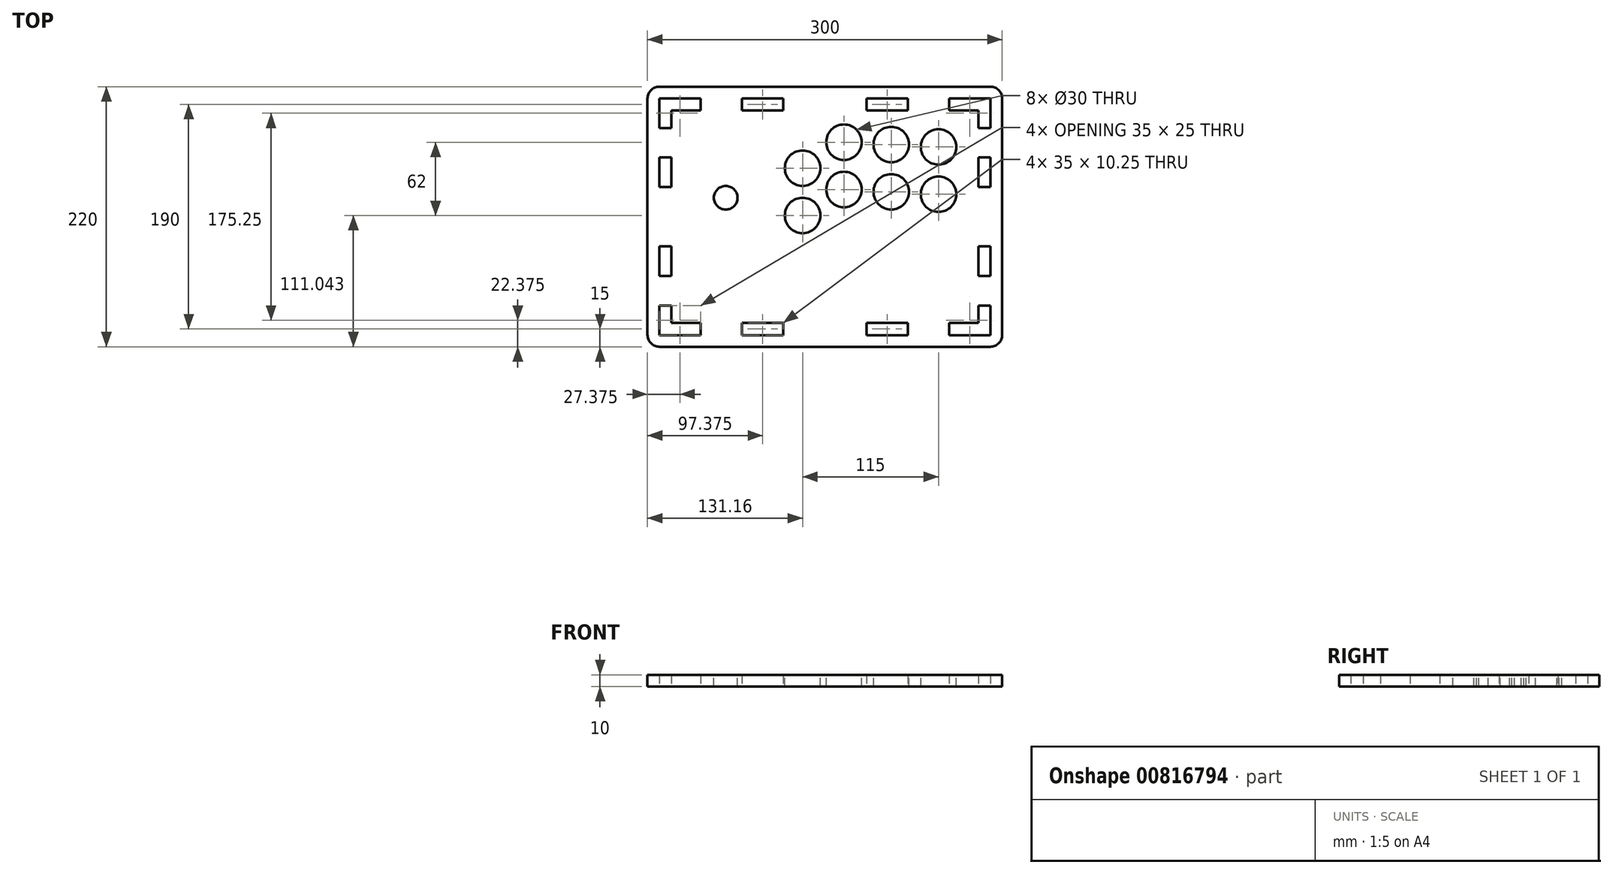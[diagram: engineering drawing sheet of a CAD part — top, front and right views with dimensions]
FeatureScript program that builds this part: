
annotation { "Feature Type Name" : "Feature", "Feature Type Description" : "" }
export const myFeature = defineFeature(function(context is Context, id is Id, definition is map)
    precondition{}
    {
        {
            var Q0;
            Q0=qCreatedBy(makeId("Top.planeOp"),FACE);
            var sketch = newSketch(context, id + "F0", { "sketchPlane" : qUnion([Q0])});
            skLineSegment(sketch, "E0.bottom", {"start": v(-140, 110) * mm, "end": v(140, 110) * mm});
            skLineSegment(sketch, "E0.top", {"start": v(-140, -110) * mm, "end": v(140, -110) * mm});
            skLineSegment(sketch, "E0.left", {"start": v(-150, 100) * mm, "end": v(-150, -100) * mm});
            skLineSegment(sketch, "E0.right", {"start": v(150, 100) * mm, "end": v(150, -100) * mm});
            skPoint(sketch, "E1.middle", {"position": v(0, 0) * mm});
            skLineSegment(sketch, "E2", {"start": v(-140.12, -100.12) * mm, "end": v(-105.13, -100.12) * mm});
            skLineSegment(sketch, "E3", {"start": v(-140.12, -100.12) * mm, "end": v(-140.13, -75.12) * mm});
            skLineSegment(sketch, "E4", {"start": v(-140.12, -75.12) * mm, "end": v(-129.88, -75.12) * mm});
            skLineSegment(sketch, "E5", {"start": v(-129.88, -75.12) * mm, "end": v(-129.88, -89.88) * mm});
            skLineSegment(sketch, "E6", {"start": v(-140.12, -50.12) * mm, "end": v(-129.88, -50.12) * mm});
            skLineSegment(sketch, "E7", {"start": v(-129.88, -50.12) * mm, "end": v(-129.88, -25.12) * mm});
            skLineSegment(sketch, "E8", {"start": v(-129.88, -25.12) * mm, "end": v(-140.12, -25.12) * mm});
            skLineSegment(sketch, "E9", {"start": v(-140.12, -25.12) * mm, "end": v(-140.12, -50.12) * mm});
            skLineSegment(sketch, "E10", {"start": v(-105.13, -100.12) * mm, "end": v(-105.13, -89.87) * mm});
            skLineSegment(sketch, "E11", {"start": v(-105.13, -89.87) * mm, "end": v(-129.88, -89.88) * mm});
            skLineSegment(sketch, "E12.MirrorCS", {"start": v(140.12, -75.12) * mm, "end": v(129.88, -75.12) * mm});
            skLineSegment(sketch, "E13.MirrorCS", {"start": v(129.88, -75.12) * mm, "end": v(129.88, -89.88) * mm});
            skLineSegment(sketch, "E14.MirrorCS", {"start": v(105.13, -89.87) * mm, "end": v(129.88, -89.88) * mm});
            skLineSegment(sketch, "E15.MirrorCS", {"start": v(105.13, -100.12) * mm, "end": v(105.13, -89.87) * mm});
            skLineSegment(sketch, "E16.MirrorCS", {"start": v(140.12, -100.12) * mm, "end": v(105.13, -100.12) * mm});
            skLineSegment(sketch, "E17.MirrorCS", {"start": v(140.12, -100.12) * mm, "end": v(140.13, -75.12) * mm});
            skLineSegment(sketch, "E18", {"start": v(-70.13, -100.12) * mm, "end": v(-70.13, -89.87) * mm});
            skLineSegment(sketch, "E19", {"start": v(-70.13, -89.87) * mm, "end": v(-35.13, -89.87) * mm});
            skLineSegment(sketch, "E20", {"start": v(-35.13, -89.87) * mm, "end": v(-35.13, -100.12) * mm});
            skLineSegment(sketch, "E21", {"start": v(-70.13, -100.12) * mm, "end": v(-35.13, -100.12) * mm});
            skLineSegment(sketch, "E22.MirrorCS", {"start": v(70.13, -89.87) * mm, "end": v(35.13, -89.87) * mm});
            skLineSegment(sketch, "E23.MirrorCS", {"start": v(70.13, -100.12) * mm, "end": v(70.13, -89.87) * mm});
            skLineSegment(sketch, "E24.MirrorCS", {"start": v(70.13, -100.12) * mm, "end": v(35.13, -100.12) * mm});
            skLineSegment(sketch, "E25.MirrorCS", {"start": v(35.13, -89.87) * mm, "end": v(35.13, -100.12) * mm});
            skLineSegment(sketch, "E26.MirrorCS", {"start": v(105.13, 100.12) * mm, "end": v(105.13, 89.87) * mm});
            skLineSegment(sketch, "E27.MirrorCS", {"start": v(-70.13, 100.12) * mm, "end": v(-70.13, 89.87) * mm});
            skLineSegment(sketch, "E28.MirrorCS", {"start": v(140.12, 75.12) * mm, "end": v(129.88, 75.12) * mm});
            skLineSegment(sketch, "E29.MirrorCS", {"start": v(70.13, 100.12) * mm, "end": v(70.13, 89.87) * mm});
            skLineSegment(sketch, "E30.MirrorCS", {"start": v(-35.13, 89.87) * mm, "end": v(-35.13, 100.12) * mm});
            skLineSegment(sketch, "E31.MirrorCS", {"start": v(-140.12, 75.12) * mm, "end": v(-129.88, 75.12) * mm});
            skLineSegment(sketch, "E32.MirrorCS", {"start": v(35.13, 89.87) * mm, "end": v(35.13, 100.12) * mm});
            skLineSegment(sketch, "E33.MirrorCS", {"start": v(-105.13, 100.12) * mm, "end": v(-105.13, 89.87) * mm});
            skLineSegment(sketch, "E34.MirrorCS", {"start": v(140.12, 100.12) * mm, "end": v(105.13, 100.12) * mm});
            skLineSegment(sketch, "E35.MirrorCS", {"start": v(-140.12, 100.12) * mm, "end": v(-140.13, 75.12) * mm});
            skLineSegment(sketch, "E36.MirrorCS", {"start": v(-70.13, 100.12) * mm, "end": v(-35.13, 100.12) * mm});
            skLineSegment(sketch, "E37.MirrorCS", {"start": v(-105.13, 89.87) * mm, "end": v(-129.88, 89.88) * mm});
            skLineSegment(sketch, "E38.MirrorCS", {"start": v(-140.12, 100.12) * mm, "end": v(-105.13, 100.12) * mm});
            skLineSegment(sketch, "E39.MirrorCS", {"start": v(-70.13, 89.87) * mm, "end": v(-35.13, 89.87) * mm});
            skLineSegment(sketch, "E40.MirrorCS", {"start": v(129.88, 75.12) * mm, "end": v(129.88, 89.88) * mm});
            skLineSegment(sketch, "E41.MirrorCS", {"start": v(70.13, 100.12) * mm, "end": v(35.13, 100.12) * mm});
            skLineSegment(sketch, "E42.MirrorCS", {"start": v(70.13, 89.87) * mm, "end": v(35.13, 89.87) * mm});
            skLineSegment(sketch, "E43.MirrorCS", {"start": v(105.13, 89.87) * mm, "end": v(129.88, 89.88) * mm});
            skLineSegment(sketch, "E44.MirrorCS", {"start": v(-129.88, 75.12) * mm, "end": v(-129.88, 89.88) * mm});
            skLineSegment(sketch, "E45.MirrorCS", {"start": v(140.12, 100.12) * mm, "end": v(140.13, 75.12) * mm});
            skLineSegment(sketch, "E46.MirrorCS", {"start": v(-129.88, 25.12) * mm, "end": v(-140.12, 25.12) * mm});
            skLineSegment(sketch, "E47.MirrorCS", {"start": v(-140.12, 25.12) * mm, "end": v(-140.12, 50.12) * mm});
            skLineSegment(sketch, "E48.MirrorCS", {"start": v(-140.12, 50.12) * mm, "end": v(-129.88, 50.12) * mm});
            skLineSegment(sketch, "E49.MirrorCS", {"start": v(-129.88, 50.12) * mm, "end": v(-129.88, 25.12) * mm});
            skLineSegment(sketch, "E50.MirrorCS", {"start": v(140.12, 50.12) * mm, "end": v(129.88, 50.12) * mm});
            skLineSegment(sketch, "E51.MirrorCS", {"start": v(140.12, 25.12) * mm, "end": v(140.12, 50.12) * mm});
            skLineSegment(sketch, "E52.MirrorCS", {"start": v(129.88, 50.12) * mm, "end": v(129.88, 25.12) * mm});
            skLineSegment(sketch, "E53.MirrorCS", {"start": v(129.88, 25.12) * mm, "end": v(140.12, 25.12) * mm});
            skLineSegment(sketch, "E54.MirrorCS", {"start": v(129.88, -25.12) * mm, "end": v(140.12, -25.12) * mm});
            skLineSegment(sketch, "E55.MirrorCS", {"start": v(140.12, -25.12) * mm, "end": v(140.12, -50.12) * mm});
            skLineSegment(sketch, "E56.MirrorCS", {"start": v(140.12, -50.12) * mm, "end": v(129.88, -50.12) * mm});
            skLineSegment(sketch, "E57.MirrorCS", {"start": v(129.88, -50.12) * mm, "end": v(129.88, -25.12) * mm});
            skPoint(sketch, "E58.visualSharp", {"position": v(-150, 110) * mm});
            skArc(sketch, "E58.filletArc", {"start": v(-140, 110) * mm, "mid": v(-147.07, 107.07) * mm, "end": v(-150, 100) * mm});
            skPoint(sketch, "E59.visualSharp", {"position": v(-150, -110) * mm});
            skArc(sketch, "E59.filletArc", {"start": v(-150, -100) * mm, "mid": v(-147.07, -107.07) * mm, "end": v(-140, -110) * mm});
            skPoint(sketch, "E60.visualSharp", {"position": v(150, -110) * mm});
            skArc(sketch, "E60.filletArc", {"start": v(140, -110) * mm, "mid": v(147.07, -107.07) * mm, "end": v(150, -100) * mm});
            skPoint(sketch, "E61.visualSharp", {"position": v(150, 110) * mm});
            skArc(sketch, "E61.filletArc", {"start": v(150, 100) * mm, "mid": v(147.07, 107.07) * mm, "end": v(140, 110) * mm});
            skSolve(sketch);
        }
        {
            var Q0;
            Q0=makeQuery(id+"F0.imprint","IMPRINT",FACE,{"disambiguationData":[TD([[makeQuery(id+"F0.imprint","IMPRINT",EDGE,{"derivedFrom":sQuery(id+"F0.wireOp",EDGE,"E0.bottom")}),-1.0]])]});
            extrude(context, id + "F1", {"entities" : qUnion([Q0]), "depth" : 10 * mm, "offsetDistance" : 25 * mm});
        }
        {
            var Q0;
            Q0=makeQuery(id+"F1.opExtrude","CAP_FACE",FACE,{"disambiguationData":[OSD([sQuery(id+"F0.wireOp",EDGE,"E0.bottom"),sQuery(id+"F0.wireOp",EDGE,"E0.top"),sQuery(id+"F0.wireOp",EDGE,"E0.left"),sQuery(id+"F0.wireOp",EDGE,"E0.right"),sQuery(id+"F0.wireOp",EDGE,"E2"),sQuery(id+"F0.wireOp",EDGE,"E3"),sQuery(id+"F0.wireOp",EDGE,"E4"),sQuery(id+"F0.wireOp",EDGE,"E5"),sQuery(id+"F0.wireOp",EDGE,"E6"),sQuery(id+"F0.wireOp",EDGE,"E7"),sQuery(id+"F0.wireOp",EDGE,"E8"),sQuery(id+"F0.wireOp",EDGE,"E9"),sQuery(id+"F0.wireOp",EDGE,"E10"),sQuery(id+"F0.wireOp",EDGE,"E11"),sQuery(id+"F0.wireOp",EDGE,"E12.MirrorCS"),sQuery(id+"F0.wireOp",EDGE,"E13.MirrorCS"),sQuery(id+"F0.wireOp",EDGE,"E14.MirrorCS"),sQuery(id+"F0.wireOp",EDGE,"E15.MirrorCS"),sQuery(id+"F0.wireOp",EDGE,"E16.MirrorCS"),sQuery(id+"F0.wireOp",EDGE,"E17.MirrorCS"),sQuery(id+"F0.wireOp",EDGE,"E18"),sQuery(id+"F0.wireOp",EDGE,"E19"),sQuery(id+"F0.wireOp",EDGE,"E20"),sQuery(id+"F0.wireOp",EDGE,"E21"),sQuery(id+"F0.wireOp",EDGE,"E22.MirrorCS"),sQuery(id+"F0.wireOp",EDGE,"E23.MirrorCS"),sQuery(id+"F0.wireOp",EDGE,"E24.MirrorCS"),sQuery(id+"F0.wireOp",EDGE,"E25.MirrorCS"),sQuery(id+"F0.wireOp",EDGE,"E26.MirrorCS"),sQuery(id+"F0.wireOp",EDGE,"E27.MirrorCS"),sQuery(id+"F0.wireOp",EDGE,"E28.MirrorCS"),sQuery(id+"F0.wireOp",EDGE,"E29.MirrorCS"),sQuery(id+"F0.wireOp",EDGE,"E30.MirrorCS"),sQuery(id+"F0.wireOp",EDGE,"E31.MirrorCS"),sQuery(id+"F0.wireOp",EDGE,"E32.MirrorCS"),sQuery(id+"F0.wireOp",EDGE,"E33.MirrorCS"),sQuery(id+"F0.wireOp",EDGE,"E34.MirrorCS"),sQuery(id+"F0.wireOp",EDGE,"E35.MirrorCS"),sQuery(id+"F0.wireOp",EDGE,"E36.MirrorCS"),sQuery(id+"F0.wireOp",EDGE,"E37.MirrorCS"),sQuery(id+"F0.wireOp",EDGE,"E38.MirrorCS"),sQuery(id+"F0.wireOp",EDGE,"E39.MirrorCS"),sQuery(id+"F0.wireOp",EDGE,"E40.MirrorCS"),sQuery(id+"F0.wireOp",EDGE,"E41.MirrorCS"),sQuery(id+"F0.wireOp",EDGE,"E42.MirrorCS"),sQuery(id+"F0.wireOp",EDGE,"E43.MirrorCS"),sQuery(id+"F0.wireOp",EDGE,"E44.MirrorCS"),sQuery(id+"F0.wireOp",EDGE,"E45.MirrorCS"),sQuery(id+"F0.wireOp",EDGE,"E46.MirrorCS"),sQuery(id+"F0.wireOp",EDGE,"E47.MirrorCS"),sQuery(id+"F0.wireOp",EDGE,"E48.MirrorCS"),sQuery(id+"F0.wireOp",EDGE,"E49.MirrorCS"),sQuery(id+"F0.wireOp",EDGE,"E50.MirrorCS"),sQuery(id+"F0.wireOp",EDGE,"E51.MirrorCS"),sQuery(id+"F0.wireOp",EDGE,"E52.MirrorCS"),sQuery(id+"F0.wireOp",EDGE,"E53.MirrorCS"),sQuery(id+"F0.wireOp",EDGE,"E54.MirrorCS"),sQuery(id+"F0.wireOp",EDGE,"E55.MirrorCS"),sQuery(id+"F0.wireOp",EDGE,"E56.MirrorCS"),sQuery(id+"F0.wireOp",EDGE,"E57.MirrorCS")])],"isStart":false});
            var sketch = newSketch(context, id + "F2", { "sketchPlane" : qUnion([Q0])});
            skLineSegment(sketch, "E62.bottom", {"start": v(-150, 110) * mm, "end": v(150, 110) * mm});
            skLineSegment(sketch, "E62.top", {"start": v(-150, -110) * mm, "end": v(150, -110) * mm});
            skLineSegment(sketch, "E62.left", {"start": v(-150, 110) * mm, "end": v(-150, -110) * mm});
            skLineSegment(sketch, "E62.right", {"start": v(150, 110) * mm, "end": v(150, -110) * mm});
            skPoint(sketch, "E62.middle", {"position": v(0, 0) * mm});
            skLineSegment(sketch, "E63", {"start": v(150, -110) * mm, "end": v(-69, -110) * mm});
            skCircle(sketch, "E64", {"center": v(96.16, 19.04) * mm, "radius": 15 * mm});
            skCircle(sketch, "E65", {"center": v(96.16, 59.04) * mm, "radius": 15 * mm});
            skCircle(sketch, "E66", {"center": v(56.16, 61.04) * mm, "radius": 15 * mm});
            skCircle(sketch, "E67", {"center": v(56.16, 21.04) * mm, "radius": 15 * mm});
            skCircle(sketch, "E68", {"center": v(16.16, 23.04) * mm, "radius": 15 * mm});
            skCircle(sketch, "E69", {"center": v(16.16, 63.04) * mm, "radius": 15 * mm});
            skCircle(sketch, "E70", {"center": v(-18.84, 1.04) * mm, "radius": 15 * mm});
            skCircle(sketch, "E71", {"center": v(-18.84, 41.04) * mm, "radius": 15 * mm});
            skCircle(sketch, "E72", {"center": v(-83.84, 16.04) * mm, "radius": 10 * mm});
            skSolve(sketch);
        }
        {
            var Q0;
            Q0=makeQuery(id+"F2.imprint","IMPRINT",FACE,{"disambiguationData":[TD([[makeQuery(id+"F2.imprint","IMPRINT",EDGE,{"derivedFrom":sQuery(id+"F2.wireOp",EDGE,"E72")}),1.0]])]});
            var Q1;
            Q1=makeQuery(id+"F2.imprint","IMPRINT",FACE,{"disambiguationData":[TD([[makeQuery(id+"F2.imprint","IMPRINT",EDGE,{"derivedFrom":sQuery(id+"F2.wireOp",EDGE,"E71")}),1.0]])]});
            var Q2;
            Q2=makeQuery(id+"F2.imprint","IMPRINT",FACE,{"disambiguationData":[TD([[makeQuery(id+"F2.imprint","IMPRINT",EDGE,{"derivedFrom":sQuery(id+"F2.wireOp",EDGE,"E69")}),1.0]])]});
            var Q3;
            Q3=makeQuery(id+"F2.imprint","IMPRINT",FACE,{"disambiguationData":[TD([[makeQuery(id+"F2.imprint","IMPRINT",EDGE,{"derivedFrom":sQuery(id+"F2.wireOp",EDGE,"E66")}),1.0]])]});
            var Q4;
            Q4=makeQuery(id+"F2.imprint","IMPRINT",FACE,{"disambiguationData":[TD([[makeQuery(id+"F2.imprint","IMPRINT",EDGE,{"derivedFrom":sQuery(id+"F2.wireOp",EDGE,"E65")}),1.0]])]});
            var Q5;
            Q5=makeQuery(id+"F2.imprint","IMPRINT",FACE,{"disambiguationData":[TD([[makeQuery(id+"F2.imprint","IMPRINT",EDGE,{"derivedFrom":sQuery(id+"F2.wireOp",EDGE,"E64")}),1.0]])]});
            var Q6;
            Q6=makeQuery(id+"F2.imprint","IMPRINT",FACE,{"disambiguationData":[TD([[makeQuery(id+"F2.imprint","IMPRINT",EDGE,{"derivedFrom":sQuery(id+"F2.wireOp",EDGE,"E67")}),1.0]])]});
            var Q7;
            Q7=makeQuery(id+"F2.imprint","IMPRINT",FACE,{"disambiguationData":[TD([[makeQuery(id+"F2.imprint","IMPRINT",EDGE,{"derivedFrom":sQuery(id+"F2.wireOp",EDGE,"E68")}),1.0]])]});
            var Q8;
            Q8=makeQuery(id+"F2.imprint","IMPRINT",FACE,{"disambiguationData":[TD([[makeQuery(id+"F2.imprint","IMPRINT",EDGE,{"derivedFrom":sQuery(id+"F2.wireOp",EDGE,"E70")}),1.0]])]});
            extrude(context, id + "F3", {"entities" : qUnion([Q0, Q1, Q2, Q3, Q4, Q5, Q6, Q7, Q8]), "operationType" : NewBodyOperationType.REMOVE, "oppositeDirection" : true, "depth" : 10 * mm, "offsetDistance" : 25 * mm});
        }
    });
